# Revit family: puz-ermp80sha_280ka12_60Hz
name_source: partatom
category: 機械設備
units: mm (PartAtom-declared; Revit-internal decimal feet)

## family parameters
OmniClass タイトル = Split System Air Conditioning Units
OmniClass 番号 = 23.75.10.24.21.27.27
パーツ タイプ = 標準
ロード時にボイドで切り取り = いいえ
丸型コネクタ寸法 = 直径を使用
作業面ベース = いいえ
共有 = いいえ
常に垂直 = はい
部屋計算ポイント = いいえ

## types (7) — shared parameters
Depth = 330  [stored 1.08268 ft]
IfcExportAs = IfcUnitaryEquipmentType
IfcExportType = AIRCONDITIONINGUNIT
OmniClassCode = 23-33 17 13 11
URL = https://www.mitsubishielectric.co.jp
Uniclass2015Code = Pr_70_65_03_84
Uniclass2015Title = Split coil remote air cooled condensing units
Uniclass2015Version = Systems v1.9
アンカーボルト位置X = 600
アンカーボルト位置Y = 370  [stored 1.21391 ft]
サービススペース = はい
ドレン管径 = 33.00 mm
ユニット数 = 1
仕様書バージョン = Version1.0
企業コード = 108420
冷媒管径 = 100.00 mm
分類コード = 50053003126100
参照している仕様書等のバージョン = 公共建築物標準仕様書（機械設備工事編）平成31年度版
周波数 = 60 Hz
呼称 = パッケージ形空気調和機_室外機
始動方式 = インバータ始動方式
形式 = パッケージ形 室外機
最大電流値 = 0 A
本体マテリアル = <カテゴリ別>
法定耐用年数 = 6
発停方法 = 付属スイッチ
積算_科目 = 1 空気調和設備
符号 = PAC
製品リリース年月 = 2022/10/11
製品出荷対象 = 国内
製造元 = 三菱電機株式会社
設置方法 = 床置形
説明 = 空冷H/P PAC インバータ室外機
負荷分類 = 1_熱源類
運転方法 = 冷暖切替
運転質量 = 0.00 kg
電動機出力_送風機 = 0 kW
電圧 = 200 V
zero-valued in all types: APF, COP, Clearance Bottom, Clearance Top, 据付ピッチ1

## per-type parameters (varying)
- PUZ-ERMP80HA12: Clearance Back=100  [stored 0.328084 ft]; Clearance Front=500; Clearance Left=10  [stored 0.0328084 ft]; Clearance Right=10  [stored 0.0328084 ft]; Height=740; Width=950; ドレン　位置X=30  [stored 0.0984252 ft]; ドレン　位置Y=111; ドレン　位置Z=23  [stored 0.0754593 ft]; ユニット2=はい; ユニット3=いいえ; 価格=721000 $; 冷媒ガス管径=15.88 mm; 冷媒液管径=9.52 mm; 冷媒管位置X=405.5  [stored 1.33038 ft]; 冷媒管位置Y=259.5; 冷媒管位置Z=295  [stored 0.967848 ft]; 冷媒管径符号=Bd; 冷媒管（ガス）位置X=434  [stored 1.42388 ft]; 冷媒管（ガス）位置Y=229  [stored 0.751312 ft]; 冷媒管（液）位置X=377  [stored 1.23688 ft]; 冷媒管（液）位置Y=290  [stored 0.951444 ft]; 冷房能力=7 kW; 形名=PUZ-ERMP-2 : PUZ-EREMP80; 推奨ブレーカー容量=20 A; 暖房能力=8 kW; 最小電線太さ_mm2=1.6; 極数=3; 構成品番=PUZ-ERMP80HA; 消費電力=2 kW; 消費電力_冷房=2 kW; 消費電力_暖房=2 kW; 相=3; 製品質量=56.00 kg; 質量=67.20 kg; 電動機出力_圧縮機=2 kW; 電源位置X=275; 電源位置Y=2  [stored 0.00656168 ft]; 電源位置Z=459  [stored 1.50591 ft]; 音響パワーレベル(dB)=70; 音響パワーレベル（冷）(dB)=68
- PUZ-ERMP112LA12: Clearance Back=150  [stored 0.492126 ft]; Clearance Front=500; Clearance Left=15  [stored 0.0492126 ft]; Clearance Right=15  [stored 0.0492126 ft]; Height=1018; Width=950; ドレン　位置X=52; ドレン　位置Y=111.4  [stored 0.365486 ft]; ドレン　位置Z=23  [stored 0.0754593 ft]; ユニット2=はい; ユニット3=いいえ; 価格=853000 $; 冷媒ガス管径=15.88 mm; 冷媒液管径=9.52 mm; 冷媒管位置X=400.5  [stored 1.31398 ft]; 冷媒管位置Y=279.75; 冷媒管位置Z=447; 冷媒管径符号=Bd; 冷媒管（ガス）位置X=429  [stored 1.40748 ft]; 冷媒管（ガス）位置Y=269  [stored 0.882546 ft]; 冷媒管（液）位置X=372  [stored 1.22047 ft]; 冷媒管（液）位置Y=290.5  [stored 0.953084 ft]; 冷房能力=10 kW; 形名=PUZ-ERMP-4 : PUZ-ERMP112; 推奨ブレーカー容量=30 A; 暖房能力=11 kW; 最小電線太さ_mm2=1.6; 極数=3; 構成品番=PUZ-ERMP112LA; 消費電力=2 kW; 消費電力_冷房=2 kW; 消費電力_暖房=2 kW; 相=3; 製品質量=67.00 kg; 質量=80.40 kg; 電動機出力_圧縮機=2 kW; 電源位置X=275; 電源位置Y=5  [stored 0.0164042 ft]; 電源位置Z=685; 音響パワーレベル(dB)=74; 音響パワーレベル（冷）(dB)=72
- PUZ-ERMP224KA2: Clearance Back=150  [stored 0.492126 ft]; Clearance Front=1000; Clearance Left=15  [stored 0.0492126 ft]; Clearance Right=15  [stored 0.0492126 ft]; Height=1338; Width=1050; ドレン　位置X=45  [stored 0.147638 ft]; ドレン　位置Y=176  [stored 0.577428 ft]; ドレン　位置Z=23  [stored 0.0754593 ft]; ユニット2=いいえ; ユニット3=はい; 価格=1565000 $; 冷媒ガス管径=25.40 mm; 冷媒液管径=9.52 mm; 冷媒管位置X=451  [stored 1.47966 ft]; 冷媒管位置Y=263  [stored 0.862861 ft]; 冷媒管位置Z=450  [stored 1.47638 ft]; 冷媒管径符号=Bg; 冷媒管（ガス）位置X=479  [stored 1.57152 ft]; 冷媒管（ガス）位置Y=236; 冷媒管（液）位置X=423  [stored 1.3878 ft]; 冷媒管（液）位置Y=290  [stored 0.951444 ft]; 冷房能力=20 kW; 形名=PUZ-ZRMP-3 : PUZ-ZRMP224KA; 推奨ブレーカー容量=40 A; 暖房能力=22 kW; 最小電線太さ_mm2=2; 極数=3; 構成品番=PUZ-ERMP224KA; 消費電力=7 kW; 消費電力_冷房=6 kW; 消費電力_暖房=7 kW; 相=3; 製品質量=106.00 kg; 質量=127.20 kg; 電動機出力_圧縮機=5 kW; 電源位置X=325  [stored 1.06627 ft]; 電源位置Y=2  [stored 0.00656168 ft]; 電源位置Z=1063; 音響パワーレベル(dB)=81; 音響パワーレベル（冷）(dB)=79
- PUZ-ERMP280KA2: Clearance Back=150  [stored 0.492126 ft]; Clearance Front=1000; Clearance Left=15  [stored 0.0492126 ft]; Clearance Right=15  [stored 0.0492126 ft]; Height=1338; Width=1050; ドレン　位置X=45  [stored 0.147638 ft]; ドレン　位置Y=176  [stored 0.577428 ft]; ドレン　位置Z=26  [stored 0.0853018 ft]; ユニット2=いいえ; ユニット3=はい; 価格=1917000 $; 冷媒ガス管径=25.40 mm; 冷媒液管径=12.70 mm; 冷媒管位置X=451  [stored 1.47966 ft]; 冷媒管位置Y=263  [stored 0.862861 ft]; 冷媒管位置Z=450  [stored 1.47638 ft]; 冷媒管径符号=Cg; 冷媒管（ガス）位置X=479  [stored 1.57152 ft]; 冷媒管（ガス）位置Y=236; 冷媒管（液）位置X=423  [stored 1.3878 ft]; 冷媒管（液）位置Y=290  [stored 0.951444 ft]; 冷房能力=25 kW; 形名=PUZ-ZRMP-3 : PUZ-ZRMP224KA; 推奨ブレーカー容量=50 A; 暖房能力=28 kW; 最小電線太さ_mm2=2; 極数=3; 構成品番=PUZ-ERMP280KA; 消費電力=9 kW; 消費電力_冷房=9 kW; 消費電力_暖房=9 kW; 相=3; 製品質量=117.00 kg; 質量=140.40 kg; 電動機出力_圧縮機=6 kW; 電源位置X=325  [stored 1.06627 ft]; 電源位置Y=2  [stored 0.00656168 ft]; 電源位置Z=1063; 音響パワーレベル(dB)=83; 音響パワーレベル（冷）(dB)=82
- PUZ-ERMP80SHA12: Clearance Back=100  [stored 0.328084 ft]; Clearance Front=500; Clearance Left=10  [stored 0.0328084 ft]; Clearance Right=10  [stored 0.0328084 ft]; Height=740; Width=950; ドレン　位置X=30  [stored 0.0984252 ft]; ドレン　位置Y=111; ドレン　位置Z=23  [stored 0.0754593 ft]; ユニット2=はい; ユニット3=いいえ; 価格=721000 $; 冷媒ガス管径=15.88 mm; 冷媒液管径=9.52 mm; 冷媒管位置X=405.5  [stored 1.33038 ft]; 冷媒管位置Y=259.5; 冷媒管位置Z=295  [stored 0.967848 ft]; 冷媒管径符号=Bd; 冷媒管（ガス）位置X=434  [stored 1.42388 ft]; 冷媒管（ガス）位置Y=229  [stored 0.751312 ft]; 冷媒管（液）位置X=377  [stored 1.23688 ft]; 冷媒管（液）位置Y=290  [stored 0.951444 ft]; 冷房能力=7 kW; 形名=PUZ-ERMP-2 : PUZ-EREMP80; 推奨ブレーカー容量=30 A; 暖房能力=8 kW; 最小電線太さ_mm2=1.6; 極数=1; 構成品番=PUZ-ERMP80SHA; 消費電力=2 kW; 消費電力_冷房=2 kW; 消費電力_暖房=2 kW; 相=1; 製品質量=59.00 kg; 質量=70.80 kg; 電動機出力_圧縮機=2 kW; 電源位置X=275; 電源位置Y=2  [stored 0.00656168 ft]; 電源位置Z=459  [stored 1.50591 ft]; 音響パワーレベル(dB)=70; 音響パワーレベル（冷）(dB)=68
- PUZ-ERMP140LA12: Clearance Back=150  [stored 0.492126 ft]; Clearance Front=500; Clearance Left=15  [stored 0.0492126 ft]; Clearance Right=15  [stored 0.0492126 ft]; Height=1018; Width=950; ドレン　位置X=52; ドレン　位置Y=111.4  [stored 0.365486 ft]; ドレン　位置Z=23  [stored 0.0754593 ft]; ユニット2=はい; ユニット3=いいえ; 価格=1010000 $; 冷媒ガス管径=15.88 mm; 冷媒液管径=9.52 mm; 冷媒管位置X=400.5  [stored 1.31398 ft]; 冷媒管位置Y=279.75; 冷媒管位置Z=447; 冷媒管径符号=Bd; 冷媒管（ガス）位置X=429  [stored 1.40748 ft]; 冷媒管（ガス）位置Y=269  [stored 0.882546 ft]; 冷媒管（液）位置X=372  [stored 1.22047 ft]; 冷媒管（液）位置Y=290.5  [stored 0.953084 ft]; 冷房能力=13 kW; 形名=PUZ-ERMP-4 : PUZ-ERMP112; 推奨ブレーカー容量=30 A; 暖房能力=14 kW; 最小電線太さ_mm2=1.6; 極数=3; 構成品番=PUZ-ERMP140LA; 消費電力=3 kW; 消費電力_冷房=3 kW; 消費電力_暖房=3 kW; 相=3; 製品質量=75.00 kg; 質量=90.00 kg; 電動機出力_圧縮機=3 kW; 電源位置X=275; 電源位置Y=5  [stored 0.0164042 ft]; 電源位置Z=685; 音響パワーレベル(dB)=74; 音響パワーレベル（冷）(dB)=73
- PUZ-ERMP160LA12: Clearance Back=150  [stored 0.492126 ft]; Clearance Front=500; Clearance Left=15  [stored 0.0492126 ft]; Clearance Right=15  [stored 0.0492126 ft]; Height=1018; Width=950; ドレン　位置X=52; ドレン　位置Y=111.4  [stored 0.365486 ft]; ドレン　位置Z=23  [stored 0.0754593 ft]; ユニット2=はい; ユニット3=いいえ; 価格=1125000 $; 冷媒ガス管径=15.88 mm; 冷媒液管径=9.52 mm; 冷媒管位置X=400.5  [stored 1.31398 ft]; 冷媒管位置Y=279.75; 冷媒管位置Z=447; 冷媒管径符号=Bd; 冷媒管（ガス）位置X=429  [stored 1.40748 ft]; 冷媒管（ガス）位置Y=269  [stored 0.882546 ft]; 冷媒管（液）位置X=372  [stored 1.22047 ft]; 冷媒管（液）位置Y=290.5  [stored 0.953084 ft]; 冷房能力=14 kW; 形名=PUZ-ERMP-4 : PUZ-ERMP112; 推奨ブレーカー容量=30 A; 暖房能力=16 kW; 最小電線太さ_mm2=1.6; 極数=3; 構成品番=PUZ-ERMP160LA; 消費電力=4 kW; 消費電力_冷房=4 kW; 消費電力_暖房=4 kW; 相=3; 製品質量=75.00 kg; 質量=90.00 kg; 電動機出力_圧縮機=4 kW; 電源位置X=275; 電源位置Y=5  [stored 0.0164042 ft]; 電源位置Z=685; 音響パワーレベル(dB)=76; 音響パワーレベル（冷）(dB)=74

note: [stored X ft] marks values corroborated as IEEE doubles in the binary element streams (Revit-internal decimal feet)
